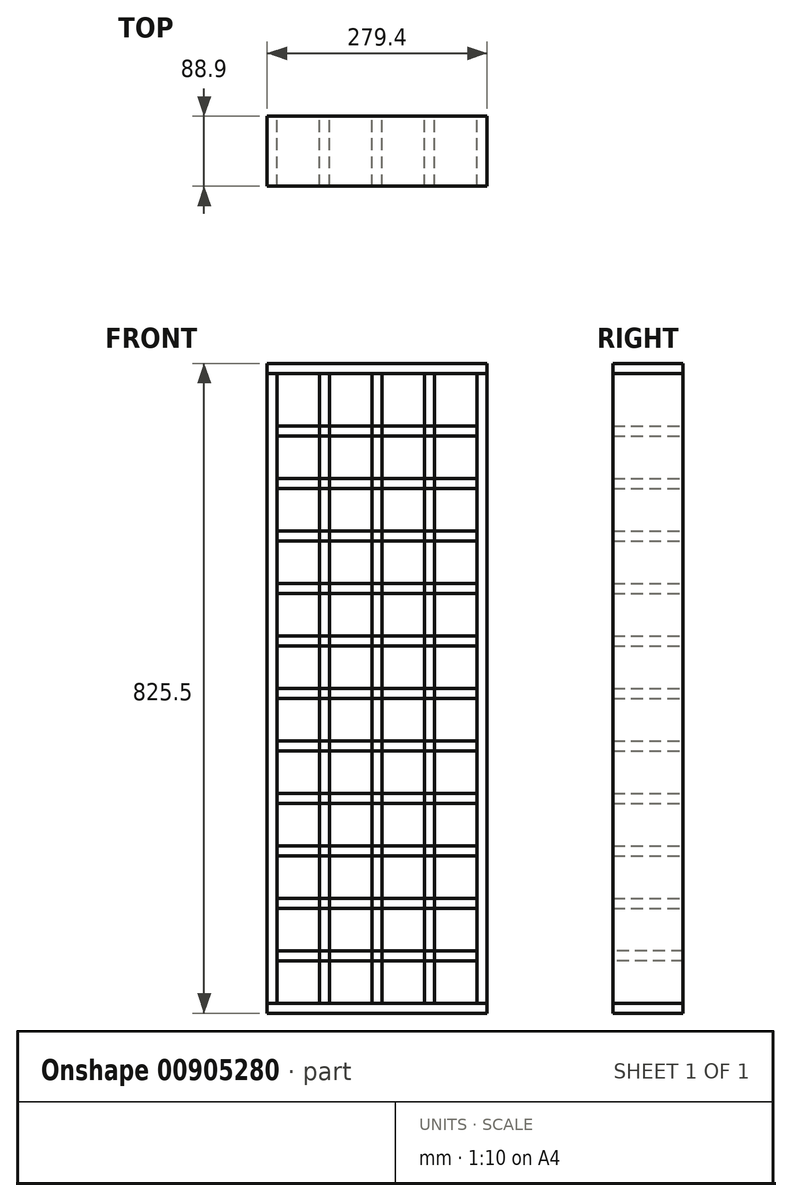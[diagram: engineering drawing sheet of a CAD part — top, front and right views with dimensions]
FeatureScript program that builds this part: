
annotation { "Feature Type Name" : "Feature", "Feature Type Description" : "" }
export const myFeature = defineFeature(function(context is Context, id is Id, definition is map)
    precondition{}
    {
        {
            var Q0;
            Q0=qCreatedBy(makeId("Top.planeOp"),FACE);
            var sketch = newSketch(context, id + "F0", { "sketchPlane" : qUnion([Q0])});
            skLineSegment(sketch, "E0", {"start": v(0, 0) * mm, "end": v(139.7, 0) * mm, "construction": true});
            skLineSegment(sketch, "E1", {"start": v(0, 0) * mm, "end": v(-139.7, 0) * mm, "construction": true});
            skLineSegment(sketch, "E2", {"start": v(-139.7, 0) * mm, "end": v(-139.7, 44.45) * mm, "construction": true});
            skLineSegment(sketch, "E3", {"start": v(-139.7, 0) * mm, "end": v(-139.7, -44.45) * mm, "construction": true});
            skLineSegment(sketch, "E4", {"start": v(139.7, 0) * mm, "end": v(139.7, 44.45) * mm, "construction": true});
            skLineSegment(sketch, "E5", {"start": v(139.7, 0) * mm, "end": v(139.7, -44.45) * mm, "construction": true});
            skLineSegment(sketch, "E6.bottom", {"start": v(-139.7, 44.45) * mm, "end": v(-127, 44.45) * mm});
            skLineSegment(sketch, "E6.top", {"start": v(-139.7, -44.45) * mm, "end": v(-127, -44.45) * mm});
            skLineSegment(sketch, "E6.left", {"start": v(-139.7, 44.45) * mm, "end": v(-139.7, -44.45) * mm});
            skLineSegment(sketch, "E6.right", {"start": v(-127, 44.45) * mm, "end": v(-127, -44.45) * mm});
            skLineSegment(sketch, "E7.bottom", {"start": v(139.7, 44.45) * mm, "end": v(127, 44.45) * mm});
            skLineSegment(sketch, "E7.top", {"start": v(139.7, -44.45) * mm, "end": v(127, -44.45) * mm});
            skLineSegment(sketch, "E7.left", {"start": v(139.7, 44.45) * mm, "end": v(139.7, -44.45) * mm});
            skLineSegment(sketch, "E7.right", {"start": v(127, 44.45) * mm, "end": v(127, -44.45) * mm});
            skLineSegment(sketch, "E8", {"start": v(-127, -44.45) * mm, "end": v(-73.03, -44.45) * mm, "construction": true});
            skLineSegment(sketch, "E9.bottom", {"start": v(-73.03, -44.45) * mm, "end": v(-60.33, -44.45) * mm});
            skLineSegment(sketch, "E9.top", {"start": v(-73.03, 44.45) * mm, "end": v(-60.33, 44.45) * mm});
            skLineSegment(sketch, "E9.left", {"start": v(-73.03, -44.45) * mm, "end": v(-73.03, 44.45) * mm});
            skLineSegment(sketch, "E9.right", {"start": v(-60.33, -44.45) * mm, "end": v(-60.33, 44.45) * mm});
            skLineSegment(sketch, "E10", {"start": v(-60.33, -44.45) * mm, "end": v(-6.35, -44.45) * mm, "construction": true});
            skLineSegment(sketch, "E11.bottom", {"start": v(-6.35, -44.45) * mm, "end": v(6.35, -44.45) * mm});
            skLineSegment(sketch, "E11.top", {"start": v(-6.35, 44.45) * mm, "end": v(6.35, 44.45) * mm});
            skLineSegment(sketch, "E11.left", {"start": v(-6.35, -44.45) * mm, "end": v(-6.35, 44.45) * mm});
            skLineSegment(sketch, "E11.right", {"start": v(6.35, -44.45) * mm, "end": v(6.35, 44.45) * mm});
            skLineSegment(sketch, "E12", {"start": v(6.35, -44.45) * mm, "end": v(60.32, -44.45) * mm, "construction": true});
            skLineSegment(sketch, "E13.bottom", {"start": v(60.32, -44.45) * mm, "end": v(73.02, -44.45) * mm});
            skLineSegment(sketch, "E13.top", {"start": v(60.32, 44.45) * mm, "end": v(73.02, 44.45) * mm});
            skLineSegment(sketch, "E13.left", {"start": v(60.32, -44.45) * mm, "end": v(60.32, 44.45) * mm});
            skLineSegment(sketch, "E13.right", {"start": v(73.02, -44.45) * mm, "end": v(73.02, 44.45) * mm});
            skSolve(sketch);
        }
        {
            var Q0;
            Q0=makeQuery(id+"F0.imprint","IMPRINT",FACE,{"disambiguationData":[TD([[makeQuery(id+"F0.imprint","IMPRINT",EDGE,{"derivedFrom":sQuery(id+"F0.wireOp",EDGE,"E6.bottom")}),-1.0]])]});
            var Q1;
            Q1=makeQuery(id+"F0.imprint","IMPRINT",FACE,{"disambiguationData":[TD([[makeQuery(id+"F0.imprint","IMPRINT",EDGE,{"derivedFrom":sQuery(id+"F0.wireOp",EDGE,"E9.bottom")}),1.0]])]});
            var Q2;
            Q2=makeQuery(id+"F0.imprint","IMPRINT",FACE,{"disambiguationData":[TD([[makeQuery(id+"F0.imprint","IMPRINT",EDGE,{"derivedFrom":sQuery(id+"F0.wireOp",EDGE,"E11.bottom")}),1.0]])]});
            var Q3;
            Q3=makeQuery(id+"F0.imprint","IMPRINT",FACE,{"disambiguationData":[TD([[makeQuery(id+"F0.imprint","IMPRINT",EDGE,{"derivedFrom":sQuery(id+"F0.wireOp",EDGE,"E7.bottom")}),1.0]])]});
            var Q4;
            Q4=makeQuery(id+"F0.imprint","IMPRINT",FACE,{"disambiguationData":[TD([[makeQuery(id+"F0.imprint","IMPRINT",EDGE,{"derivedFrom":sQuery(id+"F0.wireOp",EDGE,"E13.bottom")}),1.0]])]});
            extrude(context, id + "F1", {"entities" : qUnion([Q0, Q1, Q2, Q3, Q4]), "depth" : 800.1 * mm, "offsetDistance" : 25.4 * mm});
        }
        {
            var Q0;
            Q0=qCreatedBy(makeId("Top.planeOp"),FACE);
            var sketch = newSketch(context, id + "F2", { "sketchPlane" : qUnion([Q0])});
            skLineSegment(sketch, "E14", {"start": v(0, 0) * mm, "end": v(0, -44.45) * mm, "construction": true});
            skLineSegment(sketch, "E15", {"start": v(0, -44.45) * mm, "end": v(-139.7, -44.45) * mm, "construction": true});
            skLineSegment(sketch, "E16", {"start": v(0, 0) * mm, "end": v(0, 44.45) * mm, "construction": true});
            skLineSegment(sketch, "E17", {"start": v(0, 44.45) * mm, "end": v(139.7, 44.45) * mm, "construction": true});
            skLineSegment(sketch, "E18.bottom", {"start": v(-139.7, -44.45) * mm, "end": v(139.7, -44.45) * mm});
            skLineSegment(sketch, "E18.top", {"start": v(-139.7, 44.45) * mm, "end": v(139.7, 44.45) * mm});
            skLineSegment(sketch, "E18.left", {"start": v(-139.7, -44.45) * mm, "end": v(-139.7, 44.45) * mm});
            skLineSegment(sketch, "E18.right", {"start": v(139.7, -44.45) * mm, "end": v(139.7, 44.45) * mm});
            skSolve(sketch);
        }
        {
            var Q0;
            Q0=makeQuery(id+"F2.imprint","IMPRINT",FACE,{"disambiguationData":[TD([[makeQuery(id+"F2.imprint","IMPRINT",EDGE,{"derivedFrom":sQuery(id+"F2.wireOp",EDGE,"E18.bottom")}),1.0]])]});
            extrude(context, id + "F3", {"entities" : qUnion([Q0]), "oppositeDirection" : true, "depth" : 12.7 * mm, "offsetDistance" : 25.4 * mm});
        }
        {
            var Q0;
            Q0=makeQuery(id+"F1.opExtrude","SWEPT_FACE",FACE,{"disambiguationData":[OSD([sQuery(id+"F0.wireOp",EDGE,"E6.right")])]});
            var sketch = newSketch(context, id + "F4", { "sketchPlane" : qUnion([Q0])});
            skLineSegment(sketch, "E19", {"start": v(-44.45, 0) * mm, "end": v(-44.45, 53.97) * mm, "construction": true});
            skLineSegment(sketch, "E20.bottom", {"start": v(44.45, 53.97) * mm, "end": v(-44.45, 53.97) * mm});
            skLineSegment(sketch, "E20.top", {"start": v(44.45, 66.68) * mm, "end": v(-44.45, 66.68) * mm});
            skLineSegment(sketch, "E20.left", {"start": v(44.45, 53.97) * mm, "end": v(44.45, 66.68) * mm});
            skLineSegment(sketch, "E20.right", {"start": v(-44.45, 53.97) * mm, "end": v(-44.45, 66.68) * mm});
            skLineSegment(sketch, "E21", {"start": v(-44.45, 66.68) * mm, "end": v(-44.45, 120.65) * mm, "construction": true});
            skLineSegment(sketch, "E22.bottom", {"start": v(-44.45, 120.65) * mm, "end": v(44.45, 120.65) * mm});
            skLineSegment(sketch, "E22.top", {"start": v(-44.45, 133.35) * mm, "end": v(44.45, 133.35) * mm});
            skLineSegment(sketch, "E22.left", {"start": v(-44.45, 120.65) * mm, "end": v(-44.45, 133.35) * mm});
            skLineSegment(sketch, "E22.right", {"start": v(44.45, 120.65) * mm, "end": v(44.45, 133.35) * mm});
            skLineSegment(sketch, "E23", {"start": v(-44.45, 133.35) * mm, "end": v(-44.45, 187.33) * mm, "construction": true});
            skLineSegment(sketch, "E24", {"start": v(-44.45, 187.33) * mm, "end": v(-44.45, 254) * mm, "construction": true});
            skLineSegment(sketch, "E25.bottom", {"start": v(-44.45, 187.33) * mm, "end": v(44.45, 187.33) * mm});
            skLineSegment(sketch, "E25.top", {"start": v(-44.45, 200.03) * mm, "end": v(44.45, 200.03) * mm});
            skLineSegment(sketch, "E25.left", {"start": v(-44.45, 187.33) * mm, "end": v(-44.45, 200.03) * mm});
            skLineSegment(sketch, "E25.right", {"start": v(44.45, 187.33) * mm, "end": v(44.45, 200.03) * mm});
            skLineSegment(sketch, "E26", {"start": v(-44.45, 254) * mm, "end": v(-44.45, 320.68) * mm, "construction": true});
            skLineSegment(sketch, "E27", {"start": v(-44.45, 320.68) * mm, "end": v(-44.45, 387.35) * mm, "construction": true});
            skLineSegment(sketch, "E28.bottom", {"start": v(-44.45, 254) * mm, "end": v(44.45, 254) * mm});
            skLineSegment(sketch, "E28.top", {"start": v(-44.45, 266.7) * mm, "end": v(44.45, 266.7) * mm});
            skLineSegment(sketch, "E28.left", {"start": v(-44.45, 254) * mm, "end": v(-44.45, 266.7) * mm});
            skLineSegment(sketch, "E28.right", {"start": v(44.45, 254) * mm, "end": v(44.45, 266.7) * mm});
            skLineSegment(sketch, "E29.bottom", {"start": v(-44.45, 320.68) * mm, "end": v(44.45, 320.68) * mm});
            skLineSegment(sketch, "E29.top", {"start": v(-44.45, 333.38) * mm, "end": v(44.45, 333.38) * mm});
            skLineSegment(sketch, "E29.left", {"start": v(-44.45, 320.68) * mm, "end": v(-44.45, 333.38) * mm});
            skLineSegment(sketch, "E29.right", {"start": v(44.45, 320.68) * mm, "end": v(44.45, 333.38) * mm});
            skLineSegment(sketch, "E30", {"start": v(-44.45, 387.35) * mm, "end": v(-44.45, 454.03) * mm, "construction": true});
            skLineSegment(sketch, "E31", {"start": v(-44.45, 454.03) * mm, "end": v(-44.45, 520.7) * mm, "construction": true});
            skLineSegment(sketch, "E32", {"start": v(-44.45, 520.7) * mm, "end": v(-44.45, 587.38) * mm, "construction": true});
            skLineSegment(sketch, "E33.bottom", {"start": v(-44.45, 387.35) * mm, "end": v(44.45, 387.35) * mm});
            skLineSegment(sketch, "E33.top", {"start": v(-44.45, 400.05) * mm, "end": v(44.45, 400.05) * mm});
            skLineSegment(sketch, "E33.left", {"start": v(-44.45, 387.35) * mm, "end": v(-44.45, 400.05) * mm});
            skLineSegment(sketch, "E33.right", {"start": v(44.45, 387.35) * mm, "end": v(44.45, 400.05) * mm});
            skLineSegment(sketch, "E34.bottom", {"start": v(-44.45, 454.03) * mm, "end": v(44.45, 454.03) * mm});
            skLineSegment(sketch, "E34.top", {"start": v(-44.45, 466.73) * mm, "end": v(44.45, 466.73) * mm});
            skLineSegment(sketch, "E34.left", {"start": v(-44.45, 454.03) * mm, "end": v(-44.45, 466.73) * mm});
            skLineSegment(sketch, "E34.right", {"start": v(44.45, 454.03) * mm, "end": v(44.45, 466.73) * mm});
            skLineSegment(sketch, "E35.bottom", {"start": v(-44.45, 520.7) * mm, "end": v(44.45, 520.7) * mm});
            skLineSegment(sketch, "E35.top", {"start": v(-44.45, 533.4) * mm, "end": v(44.45, 533.4) * mm});
            skLineSegment(sketch, "E35.left", {"start": v(-44.45, 520.7) * mm, "end": v(-44.45, 533.4) * mm});
            skLineSegment(sketch, "E35.right", {"start": v(44.45, 520.7) * mm, "end": v(44.45, 533.4) * mm});
            skLineSegment(sketch, "E36", {"start": v(-44.45, 587.38) * mm, "end": v(-44.45, 654.05) * mm, "construction": true});
            skLineSegment(sketch, "E37", {"start": v(-44.45, 654.05) * mm, "end": v(-44.45, 720.73) * mm, "construction": true});
            skLineSegment(sketch, "E38.bottom", {"start": v(-44.45, 587.38) * mm, "end": v(44.45, 587.38) * mm});
            skLineSegment(sketch, "E38.top", {"start": v(-44.45, 600.08) * mm, "end": v(44.45, 600.08) * mm});
            skLineSegment(sketch, "E38.left", {"start": v(-44.45, 587.38) * mm, "end": v(-44.45, 600.08) * mm});
            skLineSegment(sketch, "E38.right", {"start": v(44.45, 587.38) * mm, "end": v(44.45, 600.08) * mm});
            skLineSegment(sketch, "E39.bottom", {"start": v(-44.45, 654.05) * mm, "end": v(44.45, 654.05) * mm});
            skLineSegment(sketch, "E39.top", {"start": v(-44.45, 666.75) * mm, "end": v(44.45, 666.75) * mm});
            skLineSegment(sketch, "E39.left", {"start": v(-44.45, 654.05) * mm, "end": v(-44.45, 666.75) * mm});
            skLineSegment(sketch, "E39.right", {"start": v(44.45, 654.05) * mm, "end": v(44.45, 666.75) * mm});
            skLineSegment(sketch, "E40.bottom", {"start": v(-44.45, 720.73) * mm, "end": v(44.45, 720.73) * mm});
            skLineSegment(sketch, "E40.top", {"start": v(-44.45, 733.43) * mm, "end": v(44.45, 733.43) * mm});
            skLineSegment(sketch, "E40.left", {"start": v(-44.45, 720.73) * mm, "end": v(-44.45, 733.43) * mm});
            skLineSegment(sketch, "E40.right", {"start": v(44.45, 720.73) * mm, "end": v(44.45, 733.43) * mm});
            skLineSegment(sketch, "E41", {"start": v(-44.45, 733.43) * mm, "end": v(-44.45, 800.1) * mm, "construction": true});
            skLineSegment(sketch, "E42.bottom", {"start": v(-44.45, 800.1) * mm, "end": v(44.45, 800.1) * mm});
            skLineSegment(sketch, "E42.top", {"start": v(-44.45, 800.1) * mm, "end": v(44.45, 800.1) * mm});
            skLineSegment(sketch, "E42.left", {"start": v(-44.45, 800.1) * mm, "end": v(-44.45, 800.1) * mm});
            skLineSegment(sketch, "E42.right", {"start": v(44.45, 800.1) * mm, "end": v(44.45, 800.1) * mm});
            skSolve(sketch);
        }
        {
            var Q0;
            Q0=makeQuery(id+"F4.imprint","IMPRINT",FACE,{"disambiguationData":[TD([[makeQuery(id+"F4.imprint","IMPRINT",EDGE,{"derivedFrom":sQuery(id+"F4.wireOp",EDGE,"E40.bottom")}),1.0]])]});
            var Q1;
            Q1=makeQuery(id+"F4.imprint","IMPRINT",FACE,{"disambiguationData":[TD([[makeQuery(id+"F4.imprint","IMPRINT",EDGE,{"derivedFrom":sQuery(id+"F4.wireOp",EDGE,"E39.bottom")}),1.0]])]});
            var Q2;
            Q2=makeQuery(id+"F4.imprint","IMPRINT",FACE,{"disambiguationData":[TD([[makeQuery(id+"F4.imprint","IMPRINT",EDGE,{"derivedFrom":sQuery(id+"F4.wireOp",EDGE,"E38.bottom")}),1.0]])]});
            var Q3;
            Q3=makeQuery(id+"F4.imprint","IMPRINT",FACE,{"disambiguationData":[TD([[makeQuery(id+"F4.imprint","IMPRINT",EDGE,{"derivedFrom":sQuery(id+"F4.wireOp",EDGE,"E35.bottom")}),1.0]])]});
            var Q4;
            Q4=makeQuery(id+"F4.imprint","IMPRINT",FACE,{"disambiguationData":[TD([[makeQuery(id+"F4.imprint","IMPRINT",EDGE,{"derivedFrom":sQuery(id+"F4.wireOp",EDGE,"E34.bottom")}),1.0]])]});
            var Q5;
            Q5=makeQuery(id+"F4.imprint","IMPRINT",FACE,{"disambiguationData":[TD([[makeQuery(id+"F4.imprint","IMPRINT",EDGE,{"derivedFrom":sQuery(id+"F4.wireOp",EDGE,"E33.bottom")}),1.0]])]});
            var Q6;
            Q6=makeQuery(id+"F4.imprint","IMPRINT",FACE,{"disambiguationData":[TD([[makeQuery(id+"F4.imprint","IMPRINT",EDGE,{"derivedFrom":sQuery(id+"F4.wireOp",EDGE,"E29.bottom")}),1.0]])]});
            var Q7;
            Q7=makeQuery(id+"F4.imprint","IMPRINT",FACE,{"disambiguationData":[TD([[makeQuery(id+"F4.imprint","IMPRINT",EDGE,{"derivedFrom":sQuery(id+"F4.wireOp",EDGE,"E28.bottom")}),1.0]])]});
            var Q8;
            Q8=makeQuery(id+"F4.imprint","IMPRINT",FACE,{"disambiguationData":[TD([[makeQuery(id+"F4.imprint","IMPRINT",EDGE,{"derivedFrom":sQuery(id+"F4.wireOp",EDGE,"E25.bottom")}),1.0]])]});
            var Q9;
            Q9=makeQuery(id+"F4.imprint","IMPRINT",FACE,{"disambiguationData":[TD([[makeQuery(id+"F4.imprint","IMPRINT",EDGE,{"derivedFrom":sQuery(id+"F4.wireOp",EDGE,"E22.bottom")}),1.0]])]});
            var Q10;
            Q10=makeQuery(id+"F4.imprint","IMPRINT",FACE,{"disambiguationData":[TD([[makeQuery(id+"F4.imprint","IMPRINT",EDGE,{"derivedFrom":sQuery(id+"F4.wireOp",EDGE,"E20.bottom")}),-1.0]])]});
            extrude(context, id + "F5", {"entities" : qUnion([Q0, Q1, Q2, Q3, Q4, Q5, Q6, Q7, Q8, Q9, Q10]), "depth" : 254 * mm, "offsetDistance" : 25.4 * mm});
        }
        {
            var Q0;
            Q0=makeQuery(id+"F1.opExtrude","CAP_FACE",FACE,{"disambiguationData":[OSD([sQuery(id+"F0.wireOp",EDGE,"E6.bottom"),sQuery(id+"F0.wireOp",EDGE,"E6.top"),sQuery(id+"F0.wireOp",EDGE,"E6.left"),sQuery(id+"F0.wireOp",EDGE,"E6.right")])],"isStart":false});
            var sketch = newSketch(context, id + "F6", { "sketchPlane" : qUnion([Q0])});
            skLineSegment(sketch, "E43.bottom", {"start": v(-139.7, -44.45) * mm, "end": v(139.7, -44.45) * mm});
            skLineSegment(sketch, "E43.top", {"start": v(-139.7, 44.45) * mm, "end": v(139.7, 44.45) * mm});
            skLineSegment(sketch, "E43.left", {"start": v(-139.7, -44.45) * mm, "end": v(-139.7, 44.45) * mm});
            skLineSegment(sketch, "E43.right", {"start": v(139.7, -44.45) * mm, "end": v(139.7, 44.45) * mm});
            skSolve(sketch);
        }
        {
            var Q0;
            {var subQ0=sQuery(id+"F6.wireOp",EDGE,"E43.left");Q0=makeQuery(id+"F6.imprint","IMPRINT",FACE,{"disambiguationData":[TD([[makeQuery(id+"F6.imprint","IMPRINT",EDGE,{"derivedFrom":subQ0}),1.0]])]});}
            var Q1;
            {var subQ2=sQuery(id+"F6.wireOp",EDGE,"E43.right");Q1=makeQuery(id+"F6.imprint","IMPRINT",FACE,{"disambiguationData":[TD([[makeQuery(id+"F6.imprint","IMPRINT",EDGE,{"derivedFrom":subQ2}),1.0]])]});}
            extrude(context, id + "F7", {"entities" : qUnion([Q0, Q1]), "depth" : 12.7 * mm, "offsetDistance" : 25.4 * mm});
        }
    });
